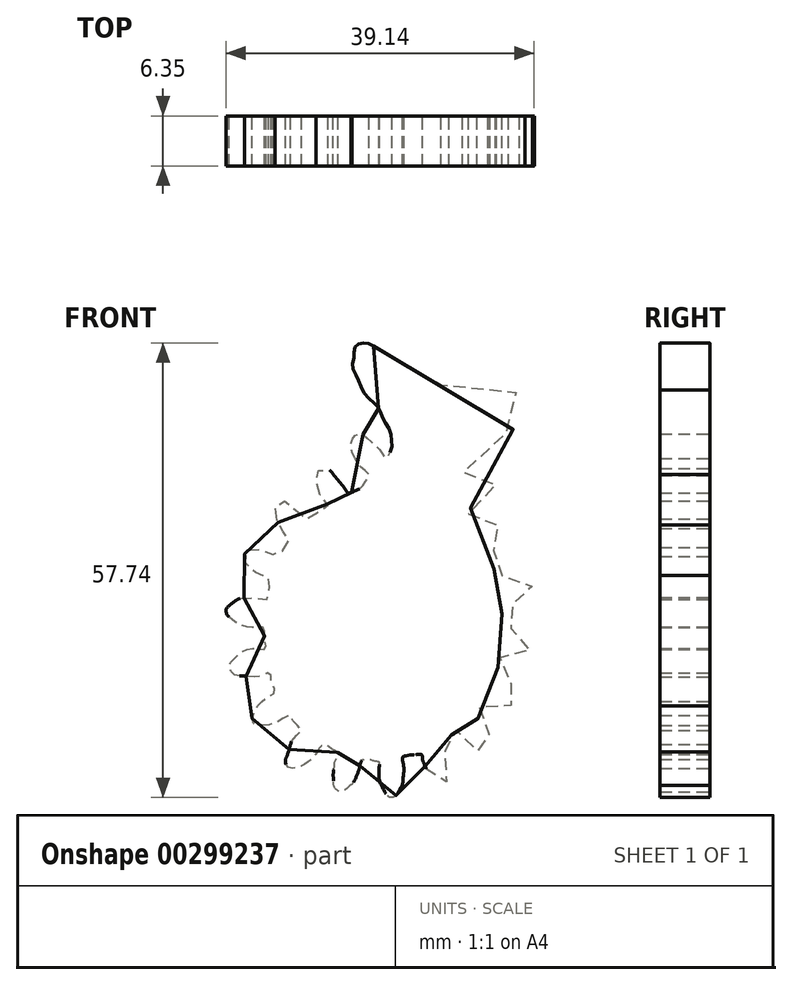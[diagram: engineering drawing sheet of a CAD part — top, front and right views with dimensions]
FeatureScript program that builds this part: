
annotation { "Feature Type Name" : "Feature", "Feature Type Description" : "" }
export const myFeature = defineFeature(function(context is Context, id is Id, definition is map)
    precondition{}
    {
        {
            var Q0;
            Q0=qCreatedBy(makeId("Front.planeOp"),FACE);
            var sketch = newSketch(context, id + "F0", { "sketchPlane" : qUnion([Q0])});
            skFitSpline(sketch, "E0", {"points": [v(22.57, 59.95) * mm, v(27.15, 56.84) * mm, v(34.87, 54.32) * mm, v(40.29, 54.23) * mm, v(41.6, 52.87) * mm, v(41.43, 50.29) * mm, v(36.66, 47.58) * mm, v(33.89, 44.72) * mm, v(34.29, 43.67) * mm, v(36.17, 43.61) * mm, v(37.8, 43.24) * mm, v(38.04, 42.14) * mm, v(37.46, 40.97) * mm, v(34.84, 39.3) * mm, v(34.66, 38.6) * mm, v(35.21, 37.46) * mm, v(35.86, 36.82) * mm, v(37.92, 37.15) * mm, v(39.27, 36.88) * mm, v(39.7, 35.43) * mm, v(38.96, 34.63) * mm, v(37.18, 33.43) * mm, v(37.43, 32.63) * mm, v(37.98, 31.46) * mm, v(38.72, 30.85) * mm, v(40.07, 30.82) * mm, v(41.24, 30.66) * mm, v(42.1, 30.2) * mm, v(42.75, 29.22) * mm, v(42, 28.54) * mm, v(41.43, 27.93) * mm, v(40.81, 27.59) * mm, v(40.32, 27.22) * mm, v(39.8, 27.03) * mm, v(39, 26.6) * mm, v(39.21, 24.66) * mm, v(40.29, 24.02) * mm, v(42.16, 23.31) * mm, v(43, 22.17) * mm, v(42.5, 21.37) * mm, v(42.04, 21.1) * mm, v(41.33, 20.88) * mm, v(39.8, 20.67) * mm, v(38.72, 20.42) * mm, v(38.2, 19.84) * mm, v(38.32, 19.22) * mm, v(38.87, 18.14) * mm, v(40.07, 17.1) * mm, v(40.66, 16.33) * mm, v(41.12, 15.16) * mm, v(40.87, 14.45) * mm, v(39.92, 14.27) * mm, v(38.29, 14.3) * mm, v(36.93, 14.8) * mm, v(36.5, 14.58) * mm, v(35.73, 13.4) * mm, v(36.1, 12.24) * mm, v(36.75, 11.53) * mm, v(37.09, 10.95) * mm, v(37.36, 10.15) * mm, v(37.3, 9.2) * mm, v(37.12, 8.6) * mm, v(36.44, 8.4) * mm, v(35.83, 8.55) * mm, v(35.09, 9.1) * mm, v(34.38, 9.53) * mm, v(33.95, 10.02) * mm, v(33.12, 11.1) * mm, v(32.38, 10.45) * mm, v(31.8, 10.18) * mm, v(31.18, 9.75) * mm, v(31.52, 8.76) * mm, v(31.95, 7.75) * mm, v(32.17, 6.7) * mm, v(32.1, 5.6) * mm, v(31.83, 4.6) * mm, v(31.09, 4.18) * mm, v(30.6, 4.52) * mm, v(30.1, 5.22) * mm, v(29.37, 6.09) * mm, v(29.03, 6.82) * mm, v(28.78, 7.56) * mm, v(28.75, 8) * mm, v(28.08, 8.05) * mm, v(27.52, 8.02) * mm, v(26.78, 7.93) * mm, v(26.32, 7.78) * mm, v(26.32, 7.1) * mm, v(26.41, 6.52) * mm, v(26.44, 5.93) * mm, v(26.32, 5.1) * mm, v(26.26, 4.27) * mm, v(25.9, 3.62) * mm, v(25.68, 3.16) * mm, v(25.25, 2.73) * mm, v(24.72, 2.6) * mm, v(24.45, 2.76) * mm, v(24.1, 3.16) * mm, v(23.7, 3.9) * mm, v(23.43, 4.45) * mm, v(23.28, 5.16) * mm, v(23.3, 5.87) * mm, v(23.3, 6.58) * mm, v(23.3, 7.07) * mm, v(22.75, 7.22) * mm, v(21.92, 7.44) * mm, v(21.43, 7.44) * mm, v(21.1, 7.28) * mm, v(20.88, 6.8) * mm, v(20.75, 6.27) * mm, v(20.57, 5.69) * mm, v(20.3, 5) * mm, v(19.86, 4.33) * mm, v(19.25, 3.84) * mm, v(18.5, 3.32) * mm, v(17.96, 3.53) * mm, v(17.56, 4.06) * mm, v(17.5, 4.82) * mm, v(17.46, 5.65) * mm, v(17.62, 6.6) * mm, v(17.7, 7.28) * mm, v(18.08, 8.15) * mm, v(17.59, 8.6) * mm, v(16.94, 8.98) * mm, v(16.6, 9.32) * mm, v(16.05, 9.22) * mm, v(15.59, 8.73) * mm, v(15.22, 8.05) * mm, v(14.76, 7.53) * mm, v(13.93, 6.89) * mm, v(13.19, 6.52) * mm, v(11.8, 6.4) * mm, v(11.37, 7.25) * mm, v(11.56, 7.84) * mm, v(11.86, 8.73) * mm, v(12.11, 9.56) * mm, v(12.66, 10.4) * mm, v(13.43, 11.07) * mm, v(12.97, 11.78) * mm, v(12.36, 12.33) * mm, v(11.99, 13.04) * mm, v(11.1, 12.67) * mm, v(9.96, 12) * mm, v(8.88, 11.78) * mm, v(7.53, 11.87) * mm, v(7.16, 12.3) * mm, v(7.25, 12.91) * mm, v(7.62, 13.9) * mm, v(8.08, 14.51) * mm, v(8.7, 15.07) * mm, v(9.59, 15.65) * mm, v(10.17, 16.02) * mm, v(9.77, 16.82) * mm, v(9.56, 17.59) * mm, v(9.47, 18.42) * mm, v(8.79, 18.27) * mm, v(7.99, 17.96) * mm, v(7.13, 17.93) * mm, v(6.24, 18.02) * mm, v(5.19, 18.08) * mm, v(4.57, 18.45) * mm, v(4.27, 19.07) * mm, v(4.42, 19.77) * mm, v(5, 20.39) * mm, v(5.56, 20.82) * mm, v(6.2, 21.31) * mm, v(7.1, 21.53) * mm, v(8.02, 21.53) * mm, v(8.82, 21.5) * mm, v(8.88, 22.17) * mm, v(8.76, 22.73) * mm, v(8.76, 23.46) * mm, v(8.63, 24.17) * mm, v(7.99, 24.23) * mm, v(7, 24.23) * mm, v(6.2, 24.33) * mm, v(5.37, 24.66) * mm, v(4.7, 25.13) * mm, v(4.27, 25.53) * mm, v(3.93, 25.9) * mm, v(3.9, 26.57) * mm, v(4.27, 27) * mm, v(4.82, 27.46) * mm, v(5.65, 27.9) * mm, v(6.3, 27.99) * mm, v(7.43, 27.99) * mm, v(8.42, 27.83) * mm, v(9.19, 27.86) * mm, v(9.25, 28.79) * mm, v(9.56, 29.65) * mm, v(9.8, 30.14) * mm, v(9.03, 30.5) * mm, v(8.05, 30.94) * mm, v(7.19, 31.46) * mm, v(6.51, 32.05) * mm, v(6.2, 33.03) * mm, v(6.3, 33.9) * mm, v(7.19, 34.35) * mm, v(7.9, 34.2) * mm, v(9.07, 33.77) * mm, v(9.83, 33.5) * mm, v(10.45, 33.25) * mm, v(10.97, 33.92) * mm, v(11.4, 34.54) * mm, v(11.86, 35.28) * mm, v(12.02, 35.55) * mm, v(11.25, 36.3) * mm, v(10.76, 36.7) * mm, v(10.45, 37.5) * mm, v(10.17, 38.5) * mm, v(10.11, 39.43) * mm, v(10.42, 40.04) * mm, v(11.03, 40.3) * mm, v(11.77, 40.08) * mm, v(12.51, 39.28) * mm, v(13.46, 38.41) * mm, v(14.05, 38.01) * mm, v(14.85, 38.32) * mm, v(15.52, 38.85) * mm, v(16.1, 39.4) * mm, v(16.79, 39.77) * mm, v(16.23, 40.41) * mm, v(15.77, 41.12) * mm, v(15.46, 42.23) * mm, v(15.3, 42.84) * mm, v(15.3, 43.64) * mm, v(15.59, 44.14) * mm, v(16.3, 44.38) * mm, v(16.9, 44.26) * mm, v(17.5, 43.64) * mm, v(18.17, 42.81) * mm, v(18.88, 41.95) * mm, v(19.43, 41.3) * mm, v(20.17, 41.52) * mm, v(21, 41.98) * mm, v(21.46, 42.6) * mm, v(21.86, 43.18) * mm, v(21.95, 43.74) * mm, v(21.22, 44.32) * mm, v(20.66, 45.06) * mm, v(20.14, 45.92) * mm, v(19.8, 46.75) * mm, v(19.74, 47.61) * mm, v(19.99, 48.32) * mm, v(20.45, 48.75) * mm, v(21.15, 48.72) * mm, v(21.77, 48.29) * mm, v(22.6, 47.52) * mm, v(23.37, 46.81) * mm, v(23.9, 46.01) * mm, v(24.17, 45.7) * mm, v(24.48, 46.01) * mm, v(24.9, 47.15) * mm, v(24.85, 48.2) * mm, v(24.66, 49.24) * mm, v(23.98, 50.35) * mm, v(23.55, 51.4) * mm, v(23.12, 52.2) * mm, v(22.48, 52.9) * mm, v(21.34, 54.07) * mm, v(20.75, 55.4) * mm, v(20.3, 56.4) * mm, v(19.86, 57.46) * mm, v(20.08, 58.44) * mm, v(20.14, 59.33) * mm, v(20.39, 60) * mm, v(21, 60.29) * mm, v(21.77, 60.32) * mm, v(22.57, 59.95) * mm]});
            skSolve(sketch);
        }
        {
            var Q0;
            Q0 = qSketchRegion(id + "F0", true);
            var Q1;
            Q1=makeQuery(id+"F0.imprint","IMPRINT",FACE,{"disambiguationData":[TD([[makeQuery(id+"F0.imprint","IMPRINT",EDGE,{"derivedFrom":sQuery(id+"F0.wireOp",EDGE,"E0")}),-1.0]])]});
            extrude(context, id + "F1", {"entities" : qUnion([Q0, Q1]), "depth" : 6.35 * mm});
        }
    });
